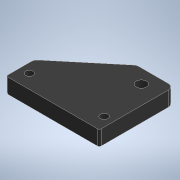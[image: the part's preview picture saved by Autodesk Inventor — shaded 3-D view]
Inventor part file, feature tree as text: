
AUTODESK INVENTOR PART (.ipt)
format: ipt  version: 2022.2 (Build 262287010, 287A)  size: 136,704 bytes
history: native  units: mm
features: sketch x4, extrude x2, hole x2, fillet x2
ambient origin geometry x8: Origin, YZ Plane, XZ Plane, XY Plane, X Axis, Y Axis, Z Axis, Center Point
bodies: Volumenkörper1 (feature_tree)
feature tree (10):
  extrude  "Extrusion1"  Depth=40.0mm
  hole  "Bohrung1"  [1 undecoded]
  hole  "Bohrung2"  [1 undecoded]
  extrude  "Extrusion2"  Depth=3.0mm
  fillet  "Rundung2"  Radius=10.0mm
  fillet  "Rundung3"  Radius=1.0mm
  sketch  "Skizze1"  dims[d0=40.0mm d1=15.0mm]
  sketch  "Skizze2"  dims[d2=50.0mm d5=20.0mm]
  sketch  "Skizze3"  dims[d6=8.0mm d7=0.0mm d8=40.0mm]
  sketch  "Skizze4"  dims[d9=5.0mm d10=4.0mm d11=7.01mm d12=6.5mm d13=3.4mm d14=90.0deg d15=8.0mm d16=20.594885mm d17=5.5mm d18=6.0mm d19=10.0mm d20=5.7mm d21=90.0deg d22=8.0mm d23=20.594885mm d24=7.5mm d26=10.0mm d27=0.0mm d28=1.0mm d29=3.0mm]
note: 2 required parameter values undecoded (feature->parameter linkage not recoverable at this tier; creation-order binding heuristic only, values carry confidence <= 0.55)
